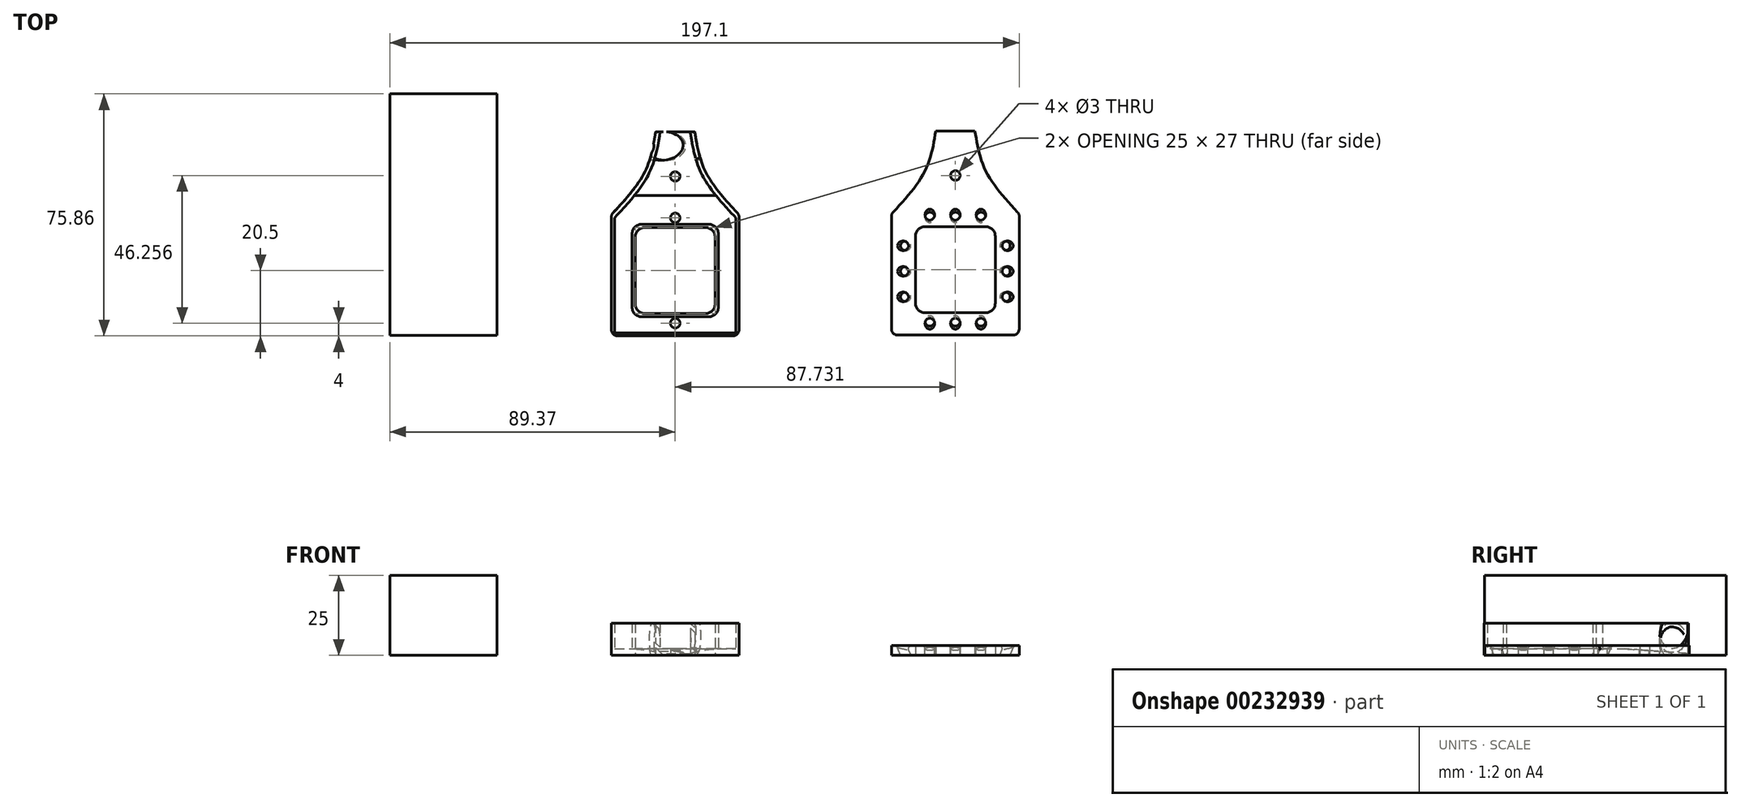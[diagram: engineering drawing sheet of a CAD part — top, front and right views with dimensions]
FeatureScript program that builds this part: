
annotation { "Feature Type Name" : "Feature", "Feature Type Description" : "" }
export const myFeature = defineFeature(function(context is Context, id is Id, definition is map)
    precondition{}
    {
        {
            var Q0;
            Q0=qCreatedBy(makeId("Top.planeOp"),FACE);
            var sketch = newSketch(context, id + "F0", { "sketchPlane" : qUnion([Q0])});
            skLineSegment(sketch, "E0.left", {"start": v(0, 0) * mm, "end": v(0, -35) * mm});
            skLineSegment(sketch, "E0.right", {"start": v(40, 0) * mm, "end": v(40, -35) * mm});
            skLineSegment(sketch, "E1", {"start": v(40, -35) * mm, "end": v(0, 0) * mm, "construction": true});
            skLineSegment(sketch, "E2.bottom", {"start": v(7.5, -31) * mm, "end": v(32.5, -31) * mm});
            skLineSegment(sketch, "E2.top", {"start": v(7.5, -4) * mm, "end": v(32.5, -4) * mm});
            skLineSegment(sketch, "E2.left", {"start": v(7.5, -31) * mm, "end": v(7.5, -4) * mm});
            skLineSegment(sketch, "E2.right", {"start": v(32.5, -31) * mm, "end": v(32.5, -4) * mm});
            skPoint(sketch, "E2.middle", {"position": v(20, -17.5) * mm});
            skLineSegment(sketch, "E3.0", {"start": v(6.5, -3) * mm, "end": v(33.5, -3) * mm});
            skLineSegment(sketch, "E3.1", {"start": v(6.5, -32) * mm, "end": v(6.5, -3) * mm});
            skLineSegment(sketch, "E3.2", {"start": v(6.5, -32) * mm, "end": v(33.5, -32) * mm});
            skLineSegment(sketch, "E3.3", {"start": v(33.5, -32) * mm, "end": v(33.5, -3) * mm});
            skLineSegment(sketch, "E4.1", {"start": v(1, -1) * mm, "end": v(1, -34) * mm});
            skLineSegment(sketch, "E4.2", {"start": v(38.86, -34) * mm, "end": v(39, -34) * mm});
            skLineSegment(sketch, "E4.3", {"start": v(39, -1) * mm, "end": v(39, -34) * mm});
            skLineSegment(sketch, "E5", {"start": v(1, -34) * mm, "end": v(1, -37) * mm});
            skLineSegment(sketch, "E6", {"start": v(1, -37) * mm, "end": v(39, -37) * mm});
            skLineSegment(sketch, "E7", {"start": v(39, -37) * mm, "end": v(39, -34) * mm});
            skLineSegment(sketch, "E8", {"start": v(0, -35) * mm, "end": v(0, -38) * mm});
            skLineSegment(sketch, "E9", {"start": v(0, -38) * mm, "end": v(40, -38) * mm});
            skLineSegment(sketch, "E10", {"start": v(40, -38) * mm, "end": v(40, -35) * mm});
            skPoint(sketch, "E11", {"position": v(20, 26) * mm});
            skPoint(sketch, "E11.positionSnap0", {"position": v(20, 0) * mm});
            skLineSegment(sketch, "E12", {"start": v(20, 26) * mm, "end": v(13.87, 26) * mm});
            skFitSpline(sketch, "E13", {"points": [v(0, 0) * mm, v(10.46, 13.38) * mm, v(13.87, 26) * mm], "startDerivative": vector(22.91, 24.62) * mm, "endDerivative": vector(4.43, 27.44) * mm});
            skLineSegment(sketch, "E14", {"start": v(20, 0) * mm, "end": v(20, 6.5) * mm, "construction": true});
            skFitSpline(sketch, "E15.MirrorCS", {"points": [v(40, 0) * mm, v(29.54, 13.38) * mm, v(26.13, 26) * mm], "startDerivative": vector(-22.91, 24.62) * mm, "endDerivative": vector(-4.43, 27.44) * mm});
            skLineSegment(sketch, "E16.MirrorCS", {"start": v(20, 26) * mm, "end": v(26.13, 26) * mm});
            skFitSpline(sketch, "E17.0", {"points": [v(38.98, -0.95) * mm, v(38.02, 0.07) * mm, v(36.58, 1.62) * mm, v(34.72, 3.7) * mm, v(33.37, 5.28) * mm, v(32.07, 6.88) * mm, v(30.86, 8.5) * mm, v(29.93, 9.89) * mm, v(29.24, 11) * mm, v(28.84, 11.71) * mm, v(28.53, 12.28) * mm, v(28.3, 12.72) * mm, v(28.1, 13.15) * mm, v(27.83, 13.73) * mm, v(27.51, 14.45) * mm, v(27.05, 15.61) * mm, v(26.56, 17.07) * mm, v(26.07, 18.83) * mm, v(25.67, 20.58) * mm, v(25.2, 22.9) * mm, v(24.93, 24.63) * mm, v(24.75, 25.78) * mm]});
            skLineSegment(sketch, "E18", {"start": v(24.75, 25.78) * mm, "end": v(24.75, 26) * mm});
            skLineSegment(sketch, "E19", {"start": v(39, -1) * mm, "end": v(38.98, -0.95) * mm});
            skFitSpline(sketch, "E20.0", {"points": [v(1.02, -0.95) * mm, v(1.98, 0.07) * mm, v(3.42, 1.62) * mm, v(5.28, 3.7) * mm, v(6.63, 5.28) * mm, v(7.93, 6.88) * mm, v(9.14, 8.5) * mm, v(10.07, 9.89) * mm, v(10.76, 11) * mm, v(11.16, 11.71) * mm, v(11.47, 12.28) * mm, v(11.7, 12.72) * mm, v(11.9, 13.15) * mm, v(12.17, 13.73) * mm, v(12.49, 14.45) * mm, v(12.95, 15.61) * mm, v(13.44, 17.07) * mm, v(13.93, 18.83) * mm, v(14.33, 20.58) * mm, v(14.8, 22.9) * mm, v(15.07, 24.63) * mm, v(15.25, 25.78) * mm]});
            skLineSegment(sketch, "E21", {"start": v(15.25, 25.78) * mm, "end": v(15.25, 26) * mm});
            skLineSegment(sketch, "E22", {"start": v(1, -1) * mm, "end": v(1.02, -0.95) * mm});
            skCircle(sketch, "E23", {"center": v(20, -34) * mm, "radius": 1.5 * mm});
            skCircle(sketch, "E24", {"center": v(20, -1) * mm, "radius": 1.5 * mm});
            skCircle(sketch, "E25", {"center": v(20, 12) * mm, "radius": 1.5 * mm});
            skSolve(sketch);
        }
        {
            var Q0;
            Q0=makeQuery(id+"F0.imprint","IMPRINT",FACE,{"disambiguationData":[TD([[makeQuery(id+"F0.imprint","IMPRINT",EDGE,{"derivedFrom":sQuery(id+"F0.wireOp",EDGE,"E3.0")}),1.0]])]});
            extrude(context, id + "F1", {"entities" : qUnion([Q0]), "depth" : 2 * mm, "offsetDistance" : 25 * mm});
        }
        {
            var Q0;
            Q0=makeQuery(id+"F0.imprint","IMPRINT",FACE,{"disambiguationData":[TD([[makeQuery(id+"F0.imprint","IMPRINT",EDGE,{"derivedFrom":sQuery(id+"F0.wireOp",EDGE,"E2.bottom")}),-1.0]])]});
            var Q1;
            Q1=makeQuery(id+"F0.imprint","IMPRINT",FACE,{"disambiguationData":[TD([[makeQuery(id+"F0.imprint","IMPRINT",EDGE,{"derivedFrom":sQuery(id+"F0.wireOp",EDGE,"E0.bottom")}),-1.0]])]});
            var Q2;
            Q2=makeQuery(id+"F0.imprint","IMPRINT",FACE,{"disambiguationData":[TD([[makeQuery(id+"F0.imprint","IMPRINT",EDGE,{"derivedFrom":sQuery(id+"F0.wireOp",EDGE,"E0.left")}),1.0]])]});
            extrude(context, id + "F2", {"entities" : qUnion([Q0, Q1, Q2]), "operationType" : NewBodyOperationType.ADD, "depth" : 10 * mm, "offsetDistance" : 25 * mm});
        }
        {
            var Q0;
            Q0=makeQuery(id+"F2.opExtrude","SWEPT_EDGE",EDGE,{"disambiguationData":[OSD([sQuery(id+"F0.wireOp",EDGE,"E2.bottom"),sQuery(id+"F0.wireOp",EDGE,"E2.right")])]});
            var Q1;
            Q1=makeQuery(id+"F2.opExtrude","SWEPT_EDGE",EDGE,{"disambiguationData":[OSD([sQuery(id+"F0.wireOp",EDGE,"E3.2"),sQuery(id+"F0.wireOp",EDGE,"E3.3")])]});
            var Q2;
            Q2=makeQuery(id+"F2.opExtrude","SWEPT_EDGE",EDGE,{"disambiguationData":[OSD([sQuery(id+"F0.wireOp",EDGE,"E3.0"),sQuery(id+"F0.wireOp",EDGE,"E3.3")])]});
            var Q3;
            Q3=makeQuery(id+"F2.opExtrude","SWEPT_EDGE",EDGE,{"disambiguationData":[OSD([sQuery(id+"F0.wireOp",EDGE,"E2.top"),sQuery(id+"F0.wireOp",EDGE,"E2.right")])]});
            var Q4;
            Q4=makeQuery(id+"F2.opExtrude","SWEPT_EDGE",EDGE,{"disambiguationData":[OSD([sQuery(id+"F0.wireOp",EDGE,"E2.top"),sQuery(id+"F0.wireOp",EDGE,"E2.left")])]});
            var Q5;
            Q5=makeQuery(id+"F2.opExtrude","SWEPT_EDGE",EDGE,{"disambiguationData":[OSD([sQuery(id+"F0.wireOp",EDGE,"E3.0"),sQuery(id+"F0.wireOp",EDGE,"E3.1")])]});
            var Q6;
            Q6=makeQuery(id+"F2.opExtrude","SWEPT_EDGE",EDGE,{"disambiguationData":[OSD([sQuery(id+"F0.wireOp",EDGE,"E3.1"),sQuery(id+"F0.wireOp",EDGE,"E3.2")])]});
            var Q7;
            Q7=makeQuery(id+"F2.opExtrude","SWEPT_EDGE",EDGE,{"disambiguationData":[OSD([sQuery(id+"F0.wireOp",EDGE,"E2.bottom"),sQuery(id+"F0.wireOp",EDGE,"E2.left")])]});
            fillet(context, id + "F3", {"entities" : qUnion([Q0, Q1, Q2, Q3, Q4, Q5, Q6, Q7]), "tangentPropagation" : true, "radius" : 3 * mm, "defaultsChanged" : true, "vertexSettings" : [], "allowEdgeOverflow" : false});
        }
        {
            var Q0;
            Q0=qCreatedBy(makeId("Top.planeOp"),FACE);
            var sketch = newSketch(context, id + "F4", { "sketchPlane" : qUnion([Q0])});
            skLineSegment(sketch, "E26.bottom", {"start": v(-35.81, -37.86) * mm, "end": v(-69.37, -37.86) * mm});
            skLineSegment(sketch, "E26.top", {"start": v(-35.81, 37.86) * mm, "end": v(-69.37, 37.86) * mm});
            skLineSegment(sketch, "E26.left", {"start": v(-35.81, -37.86) * mm, "end": v(-35.81, 37.86) * mm});
            skLineSegment(sketch, "E26.right", {"start": v(-69.37, -37.86) * mm, "end": v(-69.37, 37.86) * mm});
            skPoint(sketch, "E26.middle", {"position": v(-52.6, 0) * mm});
            skSolve(sketch);
        }
        {
            var Q0;
            Q0=makeQuery(id+"F4.imprint","IMPRINT",FACE,{"disambiguationData":[TD([[makeQuery(id+"F4.imprint","IMPRINT",EDGE,{"derivedFrom":sQuery(id+"F4.wireOp",EDGE,"E26.bottom")}),-1.0]])]});
            extrude(context, id + "F5", {"entities" : qUnion([Q0]), "depth" : 25 * mm, "offsetDistance" : 25 * mm});
        }
        {
            var Q0;
            Q0=makeQuery(id+"F5.opExtrude","CAP_EDGE",EDGE,{"disambiguationData":[OSD([sQuery(id+"F4.wireOp",EDGE,"E26.right")])],"isStart":false});
            cPlane(context, id + "F6", {"entities" : qUnion([Q0]), "cplaneType" : CPlaneType.LINE_ANGLE, "offset" : 50 * mm, "angle" : 45 * degree, "oppositeDirection" : true, "width" : 150 * mm, "height" : 150 * mm});
        }
        {
            var Q0;
            Q0=qCreatedBy(id+"F6.planeOp",FACE);
            var sketch = newSketch(context, id + "F7", { "sketchPlane" : qUnion([Q0])});
            skCircle(sketch, "E27", {"center": v(-31.53, 0) * mm, "radius": 4.5 * mm});
            skCircle(sketch, "E28.0.1.0", {"center": v(-31.53, 12) * mm, "radius": 4.5 * mm});
            skCircle(sketch, "E28.0.2.0", {"center": v(-31.53, 24) * mm, "radius": 4.5 * mm});
            skCircle(sketch, "E28.1.0.0", {"center": v(-21.53, 0) * mm, "radius": 4.5 * mm});
            skCircle(sketch, "E28.1.1.0", {"center": v(-21.53, 12) * mm, "radius": 4.5 * mm});
            skCircle(sketch, "E28.1.2.0", {"center": v(-21.53, 24) * mm, "radius": 4.5 * mm});
            skLineSegment(sketch, "E28.direction1", {"start": v(-31.53, 0) * mm, "end": v(-21.53, 0) * mm, "construction": true});
            skLineSegment(sketch, "E28.direction2", {"start": v(-31.53, 0) * mm, "end": v(-31.53, 12) * mm, "construction": true});
            skSolve(sketch);
        }
        {
            var Q0;
            Q0=makeQuery(id+"F7.imprint","IMPRINT",FACE,{"disambiguationData":[TD([[makeQuery(id+"F7.imprint","IMPRINT",EDGE,{"derivedFrom":sQuery(id+"F7.wireOp",EDGE,"E27")}),1.0]])]});
            var Q1;
            Q1=makeQuery(id+"F7.imprint","IMPRINT",FACE,{"disambiguationData":[TD([[makeQuery(id+"F7.imprint","IMPRINT",EDGE,{"derivedFrom":sQuery(id+"F7.wireOp",EDGE,"E28.1.0.0")}),1.0]])]});
            var Q2;
            Q2=makeQuery(id+"F7.imprint","IMPRINT",FACE,{"disambiguationData":[TD([[makeQuery(id+"F7.imprint","IMPRINT",EDGE,{"derivedFrom":sQuery(id+"F7.wireOp",EDGE,"E28.1.1.0")}),1.0]])]});
            var Q3;
            Q3=makeQuery(id+"F7.imprint","IMPRINT",FACE,{"disambiguationData":[TD([[makeQuery(id+"F7.imprint","IMPRINT",EDGE,{"derivedFrom":sQuery(id+"F7.wireOp",EDGE,"E28.0.1.0")}),1.0]])]});
            var Q4;
            Q4=makeQuery(id+"F7.imprint","IMPRINT",FACE,{"disambiguationData":[TD([[makeQuery(id+"F7.imprint","IMPRINT",EDGE,{"derivedFrom":sQuery(id+"F7.wireOp",EDGE,"E28.0.2.0")}),1.0]])]});
            var Q5;
            Q5=makeQuery(id+"F7.imprint","IMPRINT",FACE,{"disambiguationData":[TD([[makeQuery(id+"F7.imprint","IMPRINT",EDGE,{"derivedFrom":sQuery(id+"F7.wireOp",EDGE,"E28.1.2.0")}),1.0]])]});
            extrude(context, id + "F8", {"entities" : qUnion([Q0, Q1, Q2, Q3, Q4, Q5]), "operationType" : NewBodyOperationType.REMOVE, "oppositeDirection" : true, "depth" : 600 * mm, "offsetDistance" : 25 * mm});
        }
        {
            var Q0;
            Q0=qCreatedBy(makeId("Top.planeOp"),FACE);
            var sketch = newSketch(context, id + "F9", { "sketchPlane" : qUnion([Q0])});
            skLineSegment(sketch, "E29.left", {"start": v(87.73, 0.26) * mm, "end": v(87.73, -34.74) * mm});
            skLineSegment(sketch, "E29.right", {"start": v(127.73, 0.26) * mm, "end": v(127.73, -34.74) * mm});
            skLineSegment(sketch, "E30", {"start": v(87.73, -34.74) * mm, "end": v(87.73, -37.74) * mm});
            skLineSegment(sketch, "E31", {"start": v(87.73, -37.74) * mm, "end": v(127.73, -37.74) * mm});
            skLineSegment(sketch, "E32", {"start": v(127.73, -37.74) * mm, "end": v(127.73, -34.74) * mm});
            skLineSegment(sketch, "E33", {"start": v(107.73, 26.26) * mm, "end": v(101.6, 26.26) * mm});
            skFitSpline(sketch, "E34", {"points": [v(87.73, 0.26) * mm, v(98.19, 13.64) * mm, v(101.6, 26.26) * mm], "startDerivative": vector(22.91, 24.62) * mm, "endDerivative": vector(4.43, 27.44) * mm});
            skFitSpline(sketch, "E35.MirrorCS", {"points": [v(127.73, 0.26) * mm, v(117.27, 13.64) * mm, v(113.86, 26.26) * mm], "startDerivative": vector(-22.91, 24.62) * mm, "endDerivative": vector(-4.43, 27.44) * mm});
            skLineSegment(sketch, "E36.MirrorCS", {"start": v(107.73, 26.26) * mm, "end": v(113.86, 26.26) * mm});
            skPoint(sketch, "E37", {"position": v(107.73, -17.24) * mm});
            skPoint(sketch, "E37.positionSnap0", {"position": v(107.73, -37.74) * mm});
            skLineSegment(sketch, "E38.bottom", {"start": v(120.23, -3.74) * mm, "end": v(95.23, -3.74) * mm});
            skLineSegment(sketch, "E38.top", {"start": v(120.23, -30.74) * mm, "end": v(95.23, -30.74) * mm});
            skLineSegment(sketch, "E38.left", {"start": v(120.23, -3.74) * mm, "end": v(120.23, -30.74) * mm});
            skLineSegment(sketch, "E38.right", {"start": v(95.23, -3.74) * mm, "end": v(95.23, -30.74) * mm});
            skCircle(sketch, "E39", {"center": v(107.73, 12.26) * mm, "radius": 1.5 * mm});
            skSolve(sketch);
        }
        {
            var Q0;
            Q0=makeQuery(id+"F9.imprint","IMPRINT",FACE,{"disambiguationData":[TD([[makeQuery(id+"F9.imprint","IMPRINT",EDGE,{"derivedFrom":sQuery(id+"F9.wireOp",EDGE,"E29.left")}),1.0]])]});
            extrude(context, id + "F10", {"entities" : qUnion([Q0]), "depth" : 3 * mm, "offsetDistance" : 25 * mm});
        }
        {
            var Q0;
            Q0=makeQuery(id+"F10.opExtrude","CAP_EDGE",EDGE,{"disambiguationData":[OSD([sQuery(id+"F9.wireOp",EDGE,"E29.right"),sQuery(id+"F9.wireOp",EDGE,"E32")])],"isStart":false});
            cPlane(context, id + "F11", {"entities" : qUnion([Q0]), "cplaneType" : CPlaneType.LINE_ANGLE, "offset" : 25 * mm, "angle" : 22 * degree, "width" : 150 * mm, "height" : 150 * mm});
        }
        {
            var Q0;
            Q0=qCreatedBy(id+"F11.planeOp",FACE);
            var sketch = newSketch(context, id + "F12", { "sketchPlane" : qUnion([Q0])});
            skLineSegment(sketch, "E40.0.0", {"start": v(118.43, -37.74) * mm, "end": v(118.43, 0.26) * mm});
            skLineSegment(sketch, "E40.0.1", {"start": v(118.43, 0.26) * mm, "end": v(117.3, 0.26) * mm});
            skLineSegment(sketch, "E40.0.2", {"start": v(117.3, 0.26) * mm, "end": v(117.3, -37.74) * mm});
            skLineSegment(sketch, "E40.0.3", {"start": v(117.3, -37.74) * mm, "end": v(118.43, -37.74) * mm});
            skFitSpline(sketch, "E41.0.0", {"points": [v(93.08, 26.26) * mm, v(92.44, 21.98) * mm, v(91.07, 12.83) * mm, v(84, 4.63) * mm, v(80.22, 0.26) * mm]});
            skLineSegment(sketch, "E41.0.1", {"start": v(80.22, 0.26) * mm, "end": v(80.22, -37.74) * mm});
            skLineSegment(sketch, "E41.0.2", {"start": v(80.22, -37.74) * mm, "end": v(117.3, -37.74) * mm});
            skLineSegment(sketch, "E41.0.3", {"start": v(117.3, -37.74) * mm, "end": v(117.3, 0.26) * mm});
            skFitSpline(sketch, "E41.0.4", {"points": [v(117.3, 0.26) * mm, v(113.53, 4.63) * mm, v(106.45, 12.83) * mm, v(105.08, 21.98) * mm, v(104.44, 26.26) * mm]});
            skLineSegment(sketch, "E41.0.5", {"start": v(104.44, 26.26) * mm, "end": v(93.08, 26.26) * mm});
            skCircle(sketch, "E42", {"center": v(114.3, -25.74) * mm, "radius": 1.5 * mm});
            skCircle(sketch, "E43.0.1.0", {"center": v(114.3, -17.74) * mm, "radius": 1.5 * mm});
            skCircle(sketch, "E43.0.2.0", {"center": v(114.3, -9.74) * mm, "radius": 1.5 * mm});
            skLineSegment(sketch, "E43.direction1", {"start": v(114.3, -25.74) * mm, "end": v(139.3, -25.74) * mm, "construction": true});
            skLineSegment(sketch, "E43.direction2", {"start": v(114.3, -25.74) * mm, "end": v(114.3, -17.74) * mm, "construction": true});
            skSolve(sketch);
        }
        {
            var Q0;
            Q0=makeQuery(id+"F12.imprint","IMPRINT",FACE,{"disambiguationData":[TD([[makeQuery(id+"F12.imprint","IMPRINT",EDGE,{"derivedFrom":sQuery(id+"F12.wireOp",EDGE,"E42")}),1.0]])]});
            var Q1;
            Q1=makeQuery(id+"F12.imprint","IMPRINT",FACE,{"disambiguationData":[TD([[makeQuery(id+"F12.imprint","IMPRINT",EDGE,{"derivedFrom":sQuery(id+"F12.wireOp",EDGE,"E43.0.1.0")}),1.0]])]});
            var Q2;
            Q2=makeQuery(id+"F12.imprint","IMPRINT",FACE,{"disambiguationData":[TD([[makeQuery(id+"F12.imprint","IMPRINT",EDGE,{"derivedFrom":sQuery(id+"F12.wireOp",EDGE,"E43.0.2.0")}),1.0]])]});
            var Q3;
            Q3=makeQuery(id+"F12.imprint","IMPRINT",FACE,{"disambiguationData":[TD([[makeQuery(id+"F12.imprint","IMPRINT",EDGE,{"derivedFrom":sQuery(id+"F12.wireOp",EDGE,"E43.0.3.0")}),1.0]])]});
            var Q4;
            Q4=makeQuery(id+"F12.imprint","IMPRINT",FACE,{"disambiguationData":[TD([[makeQuery(id+"F12.imprint","IMPRINT",EDGE,{"derivedFrom":sQuery(id+"F12.wireOp",EDGE,"E43.0.4.0")}),1.0]])]});
            var Q5;
            Q5=makeQuery(id+"F12.imprint","IMPRINT",FACE,{"disambiguationData":[TD([[makeQuery(id+"F12.imprint","IMPRINT",EDGE,{"derivedFrom":sQuery(id+"F12.wireOp",EDGE,"E43.0.5.0")}),1.0]])]});
            extrude(context, id + "F13", {"entities" : qUnion([Q0, Q1, Q2, Q3, Q4, Q5]), "operationType" : NewBodyOperationType.REMOVE, "oppositeDirection" : true, "depth" : 25 * mm, "offsetDistance" : 25 * mm});
        }
        {
            var Q0;
            Q0=makeQuery(id+"F10.opExtrude","CAP_EDGE",EDGE,{"disambiguationData":[OSD([sQuery(id+"F9.wireOp",EDGE,"E29.left"),sQuery(id+"F9.wireOp",EDGE,"E30")])],"isStart":false});
            cPlane(context, id + "F14", {"entities" : qUnion([Q0]), "cplaneType" : CPlaneType.LINE_ANGLE, "offset" : 25 * mm, "angle" : 22 * degree, "width" : 150 * mm, "height" : 150 * mm});
        }
        {
            var Q0;
            Q0=qCreatedBy(id+"F14.planeOp",FACE);
            var sketch = newSketch(context, id + "F15", { "sketchPlane" : qUnion([Q0])});
            skLineSegment(sketch, "E44.0", {"start": v(82.47, -0.26) * mm, "end": v(82.47, 37.74) * mm});
            skCircle(sketch, "E45", {"center": v(85.47, 25.74) * mm, "radius": 1.5 * mm});
            skCircle(sketch, "E46.0.1.0", {"center": v(85.47, 17.74) * mm, "radius": 1.5 * mm});
            skCircle(sketch, "E46.0.2.0", {"center": v(85.47, 9.74) * mm, "radius": 1.5 * mm});
            skLineSegment(sketch, "E46.direction1", {"start": v(85.47, 25.74) * mm, "end": v(110.47, 25.74) * mm, "construction": true});
            skLineSegment(sketch, "E46.direction2", {"start": v(85.47, 25.74) * mm, "end": v(85.47, 17.74) * mm, "construction": true});
            skSolve(sketch);
        }
        {
            var Q0;
            Q0=makeQuery(id+"F15.imprint","IMPRINT",FACE,{"disambiguationData":[TD([[makeQuery(id+"F15.imprint","IMPRINT",EDGE,{"derivedFrom":sQuery(id+"F15.wireOp",EDGE,"E45")}),1.0]])]});
            var Q1;
            Q1=makeQuery(id+"F15.imprint","IMPRINT",FACE,{"disambiguationData":[TD([[makeQuery(id+"F15.imprint","IMPRINT",EDGE,{"derivedFrom":sQuery(id+"F15.wireOp",EDGE,"E46.0.1.0")}),1.0]])]});
            var Q2;
            Q2=makeQuery(id+"F15.imprint","IMPRINT",FACE,{"disambiguationData":[TD([[makeQuery(id+"F15.imprint","IMPRINT",EDGE,{"derivedFrom":sQuery(id+"F15.wireOp",EDGE,"E46.0.2.0")}),1.0]])]});
            extrude(context, id + "F16", {"entities" : qUnion([Q0, Q1, Q2]), "operationType" : NewBodyOperationType.REMOVE, "depth" : 25 * mm, "offsetDistance" : 25 * mm});
        }
        {
            var Q0;
            Q0=makeQuery(id+"F10.opExtrude","CAP_EDGE",EDGE,{"disambiguationData":[OSD([sQuery(id+"F9.wireOp",EDGE,"E31")])],"isStart":false});
            cPlane(context, id + "F17", {"entities" : qUnion([Q0]), "cplaneType" : CPlaneType.LINE_ANGLE, "offset" : 25 * mm, "angle" : 292 * degree, "width" : 150 * mm, "height" : 150 * mm});
        }
        {
            var Q0;
            Q0=qCreatedBy(id+"F17.planeOp",FACE);
            var sketch = newSketch(context, id + "F18", { "sketchPlane" : qUnion([Q0])});
            skLineSegment(sketch, "E47.0", {"start": v(87.73, 33.87) * mm, "end": v(127.73, 33.87) * mm});
            skCircle(sketch, "E48", {"center": v(99.73, 30.87) * mm, "radius": 1.5 * mm});
            skCircle(sketch, "E49.1.0.0", {"center": v(107.73, 30.87) * mm, "radius": 1.5 * mm});
            skCircle(sketch, "E49.2.0.0", {"center": v(115.73, 30.87) * mm, "radius": 1.5 * mm});
            skLineSegment(sketch, "E49.direction1", {"start": v(99.73, 30.87) * mm, "end": v(107.73, 30.87) * mm, "construction": true});
            skSolve(sketch);
        }
        {
            var Q0;
            Q0=makeQuery(id+"F18.imprint","IMPRINT",FACE,{"disambiguationData":[TD([[makeQuery(id+"F18.imprint","IMPRINT",EDGE,{"derivedFrom":sQuery(id+"F18.wireOp",EDGE,"E48")}),1.0]])]});
            var Q1;
            Q1=makeQuery(id+"F18.imprint","IMPRINT",FACE,{"disambiguationData":[TD([[makeQuery(id+"F18.imprint","IMPRINT",EDGE,{"derivedFrom":sQuery(id+"F18.wireOp",EDGE,"E49.1.0.0")}),1.0]])]});
            var Q2;
            Q2=makeQuery(id+"F18.imprint","IMPRINT",FACE,{"disambiguationData":[TD([[makeQuery(id+"F18.imprint","IMPRINT",EDGE,{"derivedFrom":sQuery(id+"F18.wireOp",EDGE,"E49.2.0.0")}),1.0]])]});
            extrude(context, id + "F19", {"entities" : qUnion([Q0, Q1, Q2]), "operationType" : NewBodyOperationType.REMOVE, "depth" : 25 * mm, "offsetDistance" : 25 * mm});
        }
        {
            var Q0;
            Q0=makeQuery(id+"F10.opExtrude","CAP_EDGE",EDGE,{"disambiguationData":[OSD([sQuery(id+"F9.wireOp",EDGE,"E33"),sQuery(id+"F9.wireOp",EDGE,"E36.MirrorCS")])],"isStart":false});
            cPlane(context, id + "F20", {"entities" : qUnion([Q0]), "cplaneType" : CPlaneType.LINE_ANGLE, "offset" : 25 * mm, "angle" : 248 * degree, "width" : 150 * mm, "height" : 150 * mm});
        }
        {
            var Q0;
            Q0=qCreatedBy(id+"F20.planeOp",FACE);
            var sketch = newSketch(context, id + "F21", { "sketchPlane" : qUnion([Q0])});
            skCircle(sketch, "E50", {"center": v(115.73, 0.78) * mm, "radius": 1.5 * mm});
            skCircle(sketch, "E51.1.0.0", {"center": v(107.73, 0.78) * mm, "radius": 1.5 * mm});
            skCircle(sketch, "E51.2.0.0", {"center": v(99.73, 0.78) * mm, "radius": 1.5 * mm});
            skLineSegment(sketch, "E51.direction1", {"start": v(115.73, 0.78) * mm, "end": v(107.73, 0.78) * mm, "construction": true});
            skSolve(sketch);
        }
        {
            var Q0;
            Q0=makeQuery(id+"F21.imprint","IMPRINT",FACE,{"disambiguationData":[TD([[makeQuery(id+"F21.imprint","IMPRINT",EDGE,{"derivedFrom":sQuery(id+"F21.wireOp",EDGE,"E51.1.0.0")}),1.0]])]});
            var Q1;
            Q1=makeQuery(id+"F21.imprint","IMPRINT",FACE,{"disambiguationData":[TD([[makeQuery(id+"F21.imprint","IMPRINT",EDGE,{"derivedFrom":sQuery(id+"F21.wireOp",EDGE,"E50")}),1.0]])]});
            var Q2;
            Q2=makeQuery(id+"F21.imprint","IMPRINT",FACE,{"disambiguationData":[TD([[makeQuery(id+"F21.imprint","IMPRINT",EDGE,{"derivedFrom":sQuery(id+"F21.wireOp",EDGE,"E51.2.0.0")}),1.0]])]});
            extrude(context, id + "F22", {"entities" : qUnion([Q0, Q1, Q2]), "operationType" : NewBodyOperationType.REMOVE, "depth" : 25 * mm, "offsetDistance" : 25 * mm});
        }
        {
            var Q0;
            Q0=makeQuery(id+"F19.boolean.opBoolean","INTERSECT",EDGE,{"derivedFrom":[makeQuery(id+"F10.opExtrude","CAP_FACE",FACE,{"disambiguationData":[OSD([sQuery(id+"F9.wireOp",EDGE,"E29.left"),sQuery(id+"F9.wireOp",EDGE,"E29.right"),sQuery(id+"F9.wireOp",EDGE,"E30"),sQuery(id+"F9.wireOp",EDGE,"E31"),sQuery(id+"F9.wireOp",EDGE,"E32"),sQuery(id+"F9.wireOp",EDGE,"E33"),sQuery(id+"F9.wireOp",EDGE,"E34"),sQuery(id+"F9.wireOp",EDGE,"E35.MirrorCS"),sQuery(id+"F9.wireOp",EDGE,"E36.MirrorCS")])],"isStart":false}),makeQuery(id+"F19.opExtrude","SWEPT_FACE",FACE,{"disambiguationData":[OSD([sQuery(id+"F18.wireOp",EDGE,"E49.2.0.0")])]})]});
            var Q1;
            Q1=makeQuery(id+"F19.boolean.opBoolean","INTERSECT",EDGE,{"derivedFrom":[makeQuery(id+"F10.opExtrude","CAP_FACE",FACE,{"disambiguationData":[OSD([sQuery(id+"F9.wireOp",EDGE,"E29.left"),sQuery(id+"F9.wireOp",EDGE,"E29.right"),sQuery(id+"F9.wireOp",EDGE,"E30"),sQuery(id+"F9.wireOp",EDGE,"E31"),sQuery(id+"F9.wireOp",EDGE,"E32"),sQuery(id+"F9.wireOp",EDGE,"E33"),sQuery(id+"F9.wireOp",EDGE,"E34"),sQuery(id+"F9.wireOp",EDGE,"E35.MirrorCS"),sQuery(id+"F9.wireOp",EDGE,"E36.MirrorCS")])],"isStart":false}),makeQuery(id+"F19.opExtrude","SWEPT_FACE",FACE,{"disambiguationData":[OSD([sQuery(id+"F18.wireOp",EDGE,"E49.1.0.0")])]})]});
            var Q2;
            Q2=makeQuery(id+"F19.boolean.opBoolean","INTERSECT",EDGE,{"derivedFrom":[makeQuery(id+"F10.opExtrude","CAP_FACE",FACE,{"disambiguationData":[OSD([sQuery(id+"F9.wireOp",EDGE,"E29.left"),sQuery(id+"F9.wireOp",EDGE,"E29.right"),sQuery(id+"F9.wireOp",EDGE,"E30"),sQuery(id+"F9.wireOp",EDGE,"E31"),sQuery(id+"F9.wireOp",EDGE,"E32"),sQuery(id+"F9.wireOp",EDGE,"E33"),sQuery(id+"F9.wireOp",EDGE,"E34"),sQuery(id+"F9.wireOp",EDGE,"E35.MirrorCS"),sQuery(id+"F9.wireOp",EDGE,"E36.MirrorCS")])],"isStart":false}),makeQuery(id+"F19.opExtrude","SWEPT_FACE",FACE,{"disambiguationData":[OSD([sQuery(id+"F18.wireOp",EDGE,"E48")])]})]});
            var Q3;
            Q3=makeQuery(id+"F16.boolean.opBoolean","INTERSECT",EDGE,{"derivedFrom":[makeQuery(id+"F10.opExtrude","CAP_FACE",FACE,{"disambiguationData":[OSD([sQuery(id+"F9.wireOp",EDGE,"E29.left"),sQuery(id+"F9.wireOp",EDGE,"E29.right"),sQuery(id+"F9.wireOp",EDGE,"E30"),sQuery(id+"F9.wireOp",EDGE,"E31"),sQuery(id+"F9.wireOp",EDGE,"E32"),sQuery(id+"F9.wireOp",EDGE,"E33"),sQuery(id+"F9.wireOp",EDGE,"E34"),sQuery(id+"F9.wireOp",EDGE,"E35.MirrorCS"),sQuery(id+"F9.wireOp",EDGE,"E36.MirrorCS")])],"isStart":false}),makeQuery(id+"F16.opExtrude","SWEPT_FACE",FACE,{"disambiguationData":[OSD([sQuery(id+"F15.wireOp",EDGE,"E45")])]})]});
            var Q4;
            Q4=makeQuery(id+"F16.boolean.opBoolean","INTERSECT",EDGE,{"derivedFrom":[makeQuery(id+"F10.opExtrude","CAP_FACE",FACE,{"disambiguationData":[OSD([sQuery(id+"F9.wireOp",EDGE,"E29.left"),sQuery(id+"F9.wireOp",EDGE,"E29.right"),sQuery(id+"F9.wireOp",EDGE,"E30"),sQuery(id+"F9.wireOp",EDGE,"E31"),sQuery(id+"F9.wireOp",EDGE,"E32"),sQuery(id+"F9.wireOp",EDGE,"E33"),sQuery(id+"F9.wireOp",EDGE,"E34"),sQuery(id+"F9.wireOp",EDGE,"E35.MirrorCS"),sQuery(id+"F9.wireOp",EDGE,"E36.MirrorCS")])],"isStart":false}),makeQuery(id+"F16.opExtrude","SWEPT_FACE",FACE,{"disambiguationData":[OSD([sQuery(id+"F15.wireOp",EDGE,"E46.0.1.0")])]})]});
            var Q5;
            Q5=makeQuery(id+"F16.boolean.opBoolean","INTERSECT",EDGE,{"derivedFrom":[makeQuery(id+"F10.opExtrude","CAP_FACE",FACE,{"disambiguationData":[OSD([sQuery(id+"F9.wireOp",EDGE,"E29.left"),sQuery(id+"F9.wireOp",EDGE,"E29.right"),sQuery(id+"F9.wireOp",EDGE,"E30"),sQuery(id+"F9.wireOp",EDGE,"E31"),sQuery(id+"F9.wireOp",EDGE,"E32"),sQuery(id+"F9.wireOp",EDGE,"E33"),sQuery(id+"F9.wireOp",EDGE,"E34"),sQuery(id+"F9.wireOp",EDGE,"E35.MirrorCS"),sQuery(id+"F9.wireOp",EDGE,"E36.MirrorCS")])],"isStart":false}),makeQuery(id+"F16.opExtrude","SWEPT_FACE",FACE,{"disambiguationData":[OSD([sQuery(id+"F15.wireOp",EDGE,"E46.0.2.0")])]})]});
            var Q6;
            Q6=makeQuery(id+"F22.boolean.opBoolean","INTERSECT",EDGE,{"derivedFrom":[makeQuery(id+"F10.opExtrude","CAP_FACE",FACE,{"disambiguationData":[OSD([sQuery(id+"F9.wireOp",EDGE,"E29.left"),sQuery(id+"F9.wireOp",EDGE,"E29.right"),sQuery(id+"F9.wireOp",EDGE,"E30"),sQuery(id+"F9.wireOp",EDGE,"E31"),sQuery(id+"F9.wireOp",EDGE,"E32"),sQuery(id+"F9.wireOp",EDGE,"E33"),sQuery(id+"F9.wireOp",EDGE,"E34"),sQuery(id+"F9.wireOp",EDGE,"E35.MirrorCS"),sQuery(id+"F9.wireOp",EDGE,"E36.MirrorCS")])],"isStart":false}),makeQuery(id+"F22.opExtrude","SWEPT_FACE",FACE,{"disambiguationData":[OSD([sQuery(id+"F21.wireOp",EDGE,"E51.2.0.0")])]})]});
            var Q7;
            Q7=makeQuery(id+"F22.boolean.opBoolean","INTERSECT",EDGE,{"derivedFrom":[makeQuery(id+"F10.opExtrude","CAP_FACE",FACE,{"disambiguationData":[OSD([sQuery(id+"F9.wireOp",EDGE,"E29.left"),sQuery(id+"F9.wireOp",EDGE,"E29.right"),sQuery(id+"F9.wireOp",EDGE,"E30"),sQuery(id+"F9.wireOp",EDGE,"E31"),sQuery(id+"F9.wireOp",EDGE,"E32"),sQuery(id+"F9.wireOp",EDGE,"E33"),sQuery(id+"F9.wireOp",EDGE,"E34"),sQuery(id+"F9.wireOp",EDGE,"E35.MirrorCS"),sQuery(id+"F9.wireOp",EDGE,"E36.MirrorCS")])],"isStart":false}),makeQuery(id+"F22.opExtrude","SWEPT_FACE",FACE,{"disambiguationData":[OSD([sQuery(id+"F21.wireOp",EDGE,"E51.1.0.0")])]})]});
            var Q8;
            Q8=makeQuery(id+"F22.boolean.opBoolean","INTERSECT",EDGE,{"derivedFrom":[makeQuery(id+"F10.opExtrude","CAP_FACE",FACE,{"disambiguationData":[OSD([sQuery(id+"F9.wireOp",EDGE,"E29.left"),sQuery(id+"F9.wireOp",EDGE,"E29.right"),sQuery(id+"F9.wireOp",EDGE,"E30"),sQuery(id+"F9.wireOp",EDGE,"E31"),sQuery(id+"F9.wireOp",EDGE,"E32"),sQuery(id+"F9.wireOp",EDGE,"E33"),sQuery(id+"F9.wireOp",EDGE,"E34"),sQuery(id+"F9.wireOp",EDGE,"E35.MirrorCS"),sQuery(id+"F9.wireOp",EDGE,"E36.MirrorCS")])],"isStart":false}),makeQuery(id+"F22.opExtrude","SWEPT_FACE",FACE,{"disambiguationData":[OSD([sQuery(id+"F21.wireOp",EDGE,"E50")])]})]});
            var Q9;
            Q9=makeQuery(id+"F13.boolean.opBoolean","INTERSECT",EDGE,{"derivedFrom":[makeQuery(id+"F10.opExtrude","CAP_FACE",FACE,{"disambiguationData":[OSD([sQuery(id+"F9.wireOp",EDGE,"E29.left"),sQuery(id+"F9.wireOp",EDGE,"E29.right"),sQuery(id+"F9.wireOp",EDGE,"E30"),sQuery(id+"F9.wireOp",EDGE,"E31"),sQuery(id+"F9.wireOp",EDGE,"E32"),sQuery(id+"F9.wireOp",EDGE,"E33"),sQuery(id+"F9.wireOp",EDGE,"E34"),sQuery(id+"F9.wireOp",EDGE,"E35.MirrorCS"),sQuery(id+"F9.wireOp",EDGE,"E36.MirrorCS")])],"isStart":false}),makeQuery(id+"F13.opExtrude","SWEPT_FACE",FACE,{"disambiguationData":[OSD([sQuery(id+"F12.wireOp",EDGE,"E43.0.2.0")])]})]});
            var Q10;
            Q10=makeQuery(id+"F13.boolean.opBoolean","INTERSECT",EDGE,{"derivedFrom":[makeQuery(id+"F10.opExtrude","CAP_FACE",FACE,{"disambiguationData":[OSD([sQuery(id+"F9.wireOp",EDGE,"E29.left"),sQuery(id+"F9.wireOp",EDGE,"E29.right"),sQuery(id+"F9.wireOp",EDGE,"E30"),sQuery(id+"F9.wireOp",EDGE,"E31"),sQuery(id+"F9.wireOp",EDGE,"E32"),sQuery(id+"F9.wireOp",EDGE,"E33"),sQuery(id+"F9.wireOp",EDGE,"E34"),sQuery(id+"F9.wireOp",EDGE,"E35.MirrorCS"),sQuery(id+"F9.wireOp",EDGE,"E36.MirrorCS")])],"isStart":false}),makeQuery(id+"F13.opExtrude","SWEPT_FACE",FACE,{"disambiguationData":[OSD([sQuery(id+"F12.wireOp",EDGE,"E43.0.1.0")])]})]});
            var Q11;
            Q11=makeQuery(id+"F13.boolean.opBoolean","INTERSECT",EDGE,{"derivedFrom":[makeQuery(id+"F10.opExtrude","CAP_FACE",FACE,{"disambiguationData":[OSD([sQuery(id+"F9.wireOp",EDGE,"E29.left"),sQuery(id+"F9.wireOp",EDGE,"E29.right"),sQuery(id+"F9.wireOp",EDGE,"E30"),sQuery(id+"F9.wireOp",EDGE,"E31"),sQuery(id+"F9.wireOp",EDGE,"E32"),sQuery(id+"F9.wireOp",EDGE,"E33"),sQuery(id+"F9.wireOp",EDGE,"E34"),sQuery(id+"F9.wireOp",EDGE,"E35.MirrorCS"),sQuery(id+"F9.wireOp",EDGE,"E36.MirrorCS")])],"isStart":false}),makeQuery(id+"F13.opExtrude","SWEPT_FACE",FACE,{"disambiguationData":[OSD([sQuery(id+"F12.wireOp",EDGE,"E42")])]})]});
            fillet(context, id + "F23", {"entities" : qUnion([Q0, Q1, Q2, Q3, Q4, Q5, Q6, Q7, Q8, Q9, Q10, Q11]), "tangentPropagation" : true, "radius" : 1 * mm, "defaultsChanged" : false, "vertexSettings" : [], "allowEdgeOverflow" : false});
        }
        {
            var Q0;
            Q0=makeQuery(id+"F1.opExtrude","CAP_EDGE",EDGE,{"disambiguationData":[OSD([sQuery(id+"F0.wireOp",EDGE,"E12"),sQuery(id+"F0.wireOp",EDGE,"E16.MirrorCS")])],"isStart":false});
            chamfer(context, id + "F24", {"entities" : qUnion([Q0]), "chamferType" : ChamferType.TWO_OFFSETS, "width1" : 1.5 * mm, "oppositeDirection" : false, "width2" : 20 * mm, "tangentPropagation" : true});
        }
        {
            var Q0;
            Q0=makeQuery(id+"F2.opExtrude","SWEPT_EDGE",EDGE,{"disambiguationData":[OSD([sQuery(id+"F0.wireOp",EDGE,"E0.right"),sQuery(id+"F0.wireOp",EDGE,"E15.MirrorCS")])]});
            var Q1;
            Q1=makeQuery(id+"F2.opExtrude","SWEPT_EDGE",EDGE,{"disambiguationData":[OSD([sQuery(id+"F0.wireOp",EDGE,"E9"),sQuery(id+"F0.wireOp",EDGE,"E10")])]});
            var Q2;
            Q2=makeQuery(id+"F2.opExtrude","SWEPT_EDGE",EDGE,{"disambiguationData":[OSD([sQuery(id+"F0.wireOp",EDGE,"E8"),sQuery(id+"F0.wireOp",EDGE,"E9")])]});
            var Q3;
            Q3=makeQuery(id+"F2.opExtrude","SWEPT_EDGE",EDGE,{"disambiguationData":[OSD([sQuery(id+"F0.wireOp",EDGE,"E0.left"),sQuery(id+"F0.wireOp",EDGE,"E13")])]});
            var Q4;
            Q4=makeQuery(id+"F10.opExtrude","SWEPT_EDGE",EDGE,{"disambiguationData":[OSD([sQuery(id+"F9.wireOp",EDGE,"E29.right"),sQuery(id+"F9.wireOp",EDGE,"E35.MirrorCS")])]});
            var Q5;
            Q5=makeQuery(id+"F10.opExtrude","SWEPT_EDGE",EDGE,{"disambiguationData":[OSD([sQuery(id+"F9.wireOp",EDGE,"E29.left"),sQuery(id+"F9.wireOp",EDGE,"E34")])]});
            var Q6;
            Q6=makeQuery(id+"F10.opExtrude","SWEPT_EDGE",EDGE,{"disambiguationData":[OSD([sQuery(id+"F9.wireOp",EDGE,"E30"),sQuery(id+"F9.wireOp",EDGE,"E31")])]});
            var Q7;
            Q7=makeQuery(id+"F10.opExtrude","SWEPT_EDGE",EDGE,{"disambiguationData":[OSD([sQuery(id+"F9.wireOp",EDGE,"E31"),sQuery(id+"F9.wireOp",EDGE,"E32")])]});
            fillet(context, id + "F25", {"entities" : qUnion([Q0, Q1, Q2, Q3, Q4, Q5, Q6, Q7]), "tangentPropagation" : true, "radius" : 2 * mm, "defaultsChanged" : false, "vertexSettings" : [], "allowEdgeOverflow" : false});
        }
        {
            var Q0;
            Q0=makeQuery(id+"F10.opExtrude","SWEPT_EDGE",EDGE,{"disambiguationData":[OSD([sQuery(id+"F9.wireOp",EDGE,"E38.top"),sQuery(id+"F9.wireOp",EDGE,"E38.left")])]});
            var Q1;
            Q1=makeQuery(id+"F10.opExtrude","SWEPT_EDGE",EDGE,{"disambiguationData":[OSD([sQuery(id+"F9.wireOp",EDGE,"E38.top"),sQuery(id+"F9.wireOp",EDGE,"E38.right")])]});
            var Q2;
            Q2=makeQuery(id+"F10.opExtrude","SWEPT_EDGE",EDGE,{"disambiguationData":[OSD([sQuery(id+"F9.wireOp",EDGE,"E38.bottom"),sQuery(id+"F9.wireOp",EDGE,"E38.right")])]});
            var Q3;
            Q3=makeQuery(id+"F10.opExtrude","SWEPT_EDGE",EDGE,{"disambiguationData":[OSD([sQuery(id+"F9.wireOp",EDGE,"E38.bottom"),sQuery(id+"F9.wireOp",EDGE,"E38.left")])]});
            fillet(context, id + "F26", {"entities" : qUnion([Q0, Q1, Q2, Q3]), "tangentPropagation" : true, "radius" : 3 * mm, "defaultsChanged" : true, "vertexSettings" : [], "allowEdgeOverflow" : false});
        }
    });
